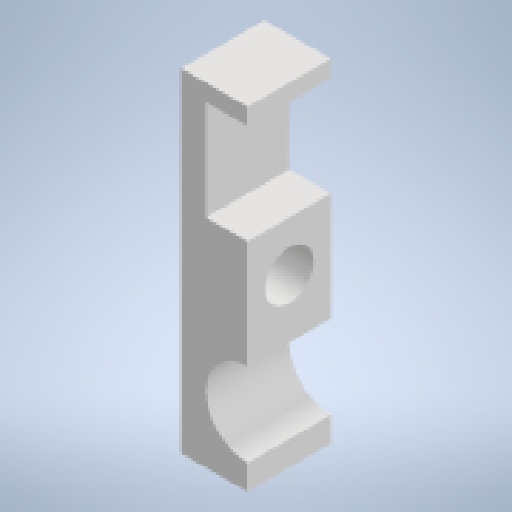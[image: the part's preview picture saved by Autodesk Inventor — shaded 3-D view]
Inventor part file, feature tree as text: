
AUTODESK INVENTOR PART (.ipt)
format: ipt  version: 2023 (Build 270158000, 158)  size: 170,496 bytes
history: native  units: mm
features: extrude x3, sketch x3
ambient origin geometry x8: Origin, YZ Plane, XZ Plane, XY Plane, X Axis, Y Axis, Z Axis, Center Point
bodies: Solid1 (feature_tree)
feature tree (6):
  extrude  "Extrusion1"  Depth=4.0mm
  extrude  "Extrusion2"  Depth=5.0mm
  extrude  "Extrusion3"  Depth=4.0mm
  sketch  "Sketch1"  dims[d0=20.0mm d1=4.0mm]
  sketch  "Sketch3"  dims[d2=5.0mm d3=5.0mm]
  sketch  "Sketch4"  dims[d4=4.0mm d5=4.0mm d6=3.0mm d7=3.0mm d8=5.0mm d9=0.0mm d10=10.0mm d11=2.5mm d12=20.0mm d13=2.7mm d14=20.0mm d15=0.0mm d16=4.0mm d17=2.0mm d18=0.0mm]
